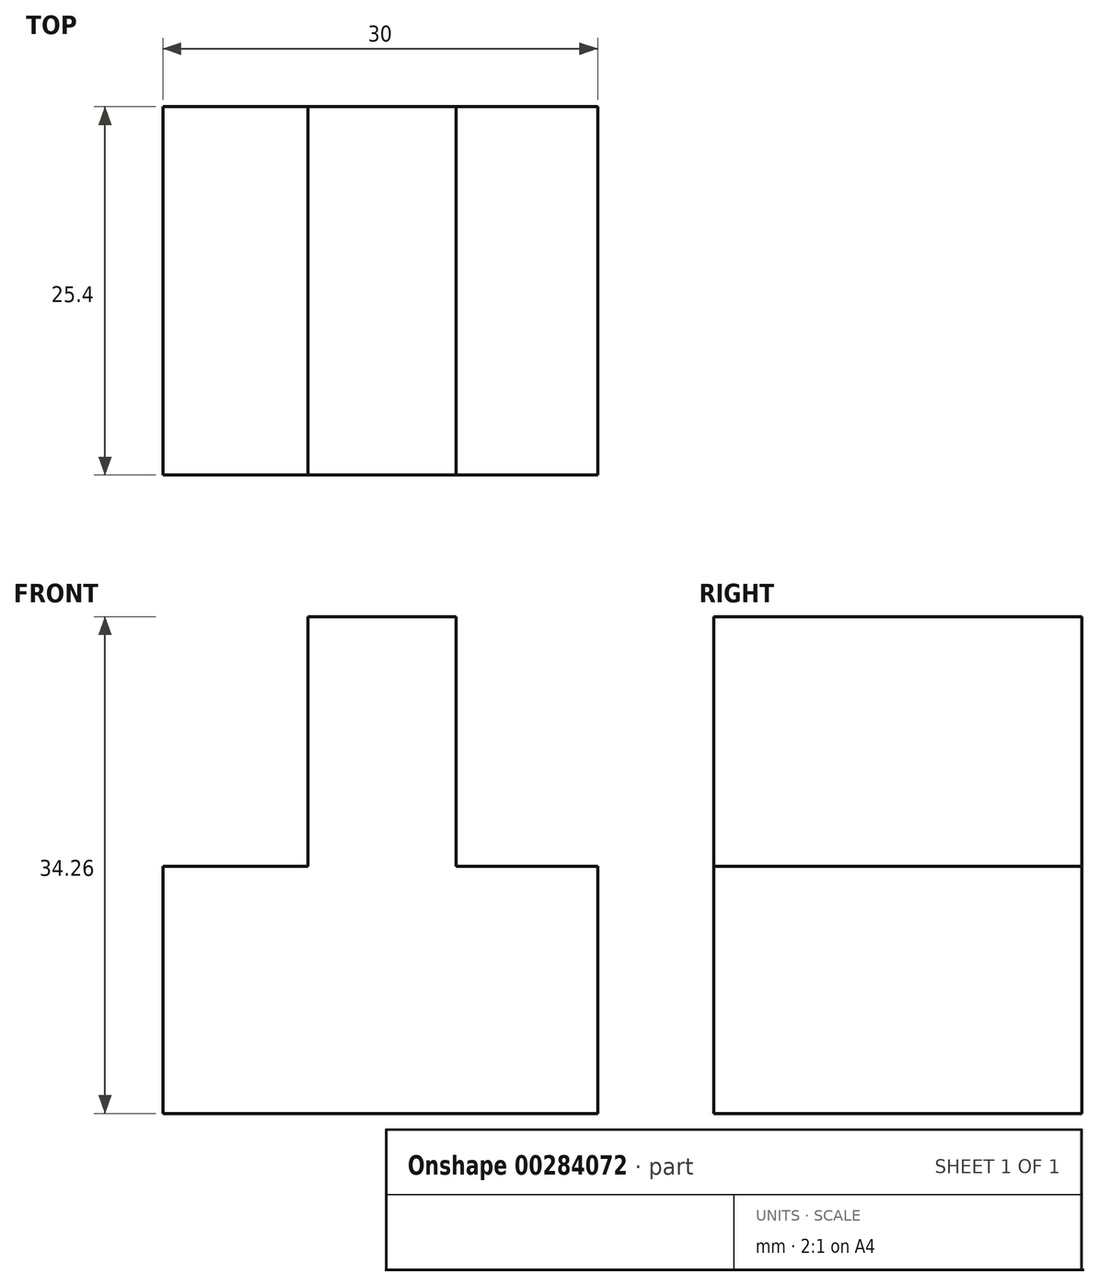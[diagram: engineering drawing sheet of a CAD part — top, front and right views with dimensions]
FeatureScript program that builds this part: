
annotation { "Feature Type Name" : "Feature", "Feature Type Description" : "" }
export const myFeature = defineFeature(function(context is Context, id is Id, definition is map)
    precondition{}
    {
        {
            var Q0;
            Q0=qCreatedBy(makeId("Front.planeOp"),FACE);
            var sketch = newSketch(context, id + "F0", { "sketchPlane" : qUnion([Q0])});
            skLineSegment(sketch, "E0", {"start": v(-52.24, 0) * mm, "end": v(-52.24, 17.02) * mm});
            skLineSegment(sketch, "E1", {"start": v(-52.24, 17.02) * mm, "end": v(-42.24, 17.02) * mm});
            skLineSegment(sketch, "E2", {"start": v(-42.24, 17.02) * mm, "end": v(-42.24, 34.26) * mm});
            skLineSegment(sketch, "E3", {"start": v(-42.24, 34.26) * mm, "end": v(-32.03, 34.26) * mm});
            skLineSegment(sketch, "E4", {"start": v(-32.03, 34.26) * mm, "end": v(-32.03, 17.02) * mm});
            skLineSegment(sketch, "E5", {"start": v(-32.03, 17.02) * mm, "end": v(-22.24, 17.02) * mm});
            skLineSegment(sketch, "E6", {"start": v(-22.24, 17.02) * mm, "end": v(-22.24, 0) * mm});
            skLineSegment(sketch, "E7", {"start": v(-22.24, 0) * mm, "end": v(-52.24, 0) * mm});
            skSolve(sketch);
        }
        {
            var Q0;
            Q0 = qSketchRegion(id + "F0", true);
            extrude(context, id + "F1", {"entities" : qUnion([Q0]), "depth" : 25.4 * mm});
        }
    });
